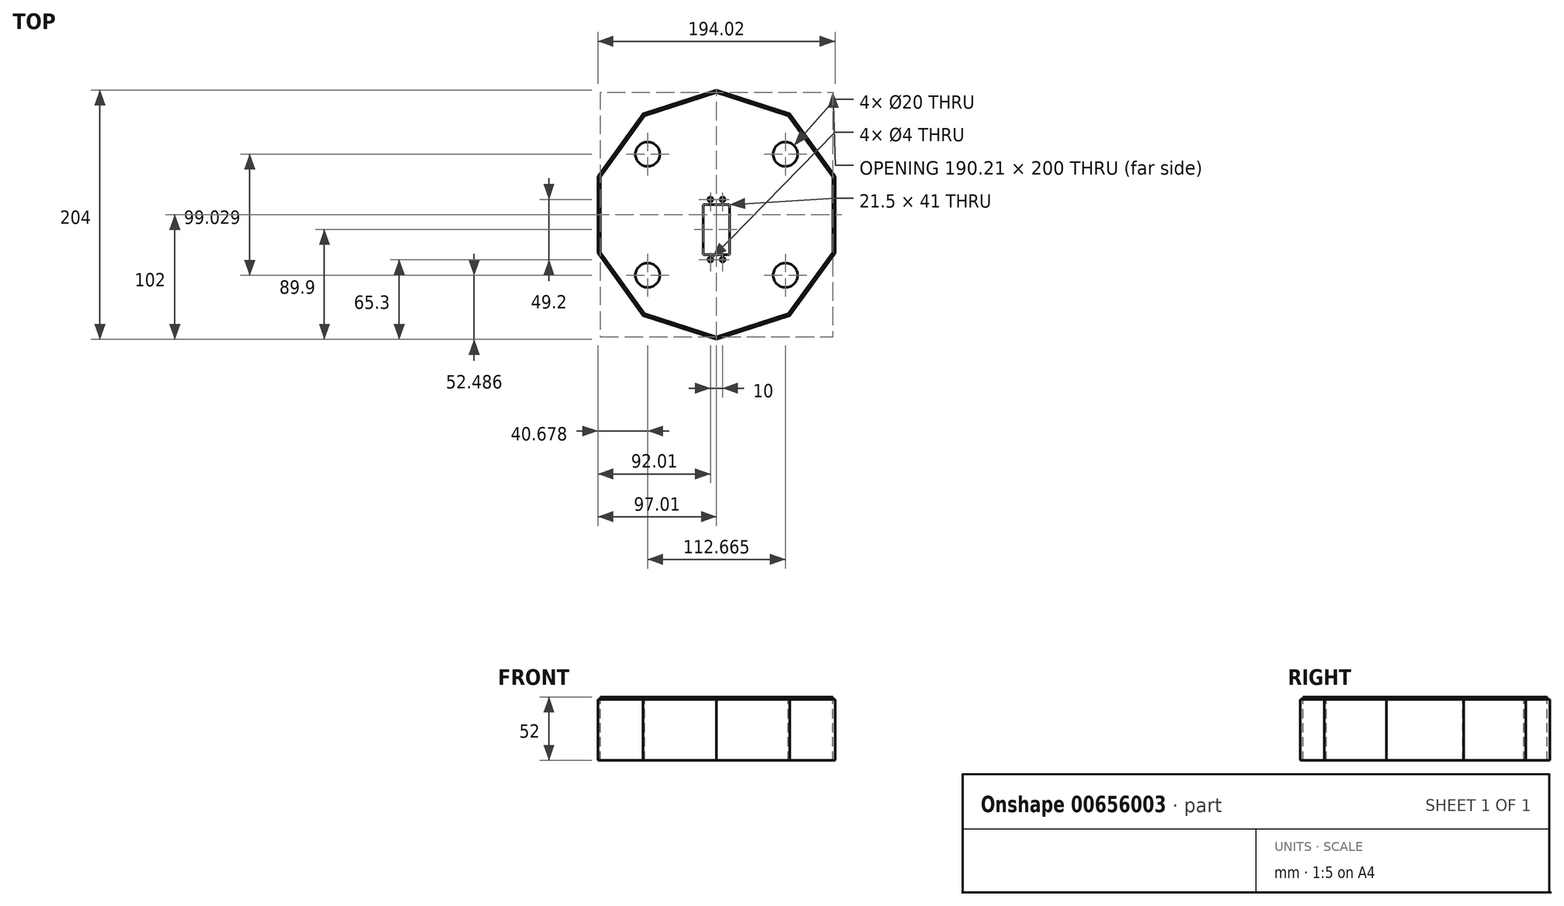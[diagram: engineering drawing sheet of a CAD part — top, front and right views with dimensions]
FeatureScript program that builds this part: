
annotation { "Feature Type Name" : "Feature", "Feature Type Description" : "" }
export const myFeature = defineFeature(function(context is Context, id is Id, definition is map)
    precondition{}
    {
        {
            var Q0;
            Q0=qCreatedBy(makeId("Top.planeOp"),FACE);
            var sketch = newSketch(context, id + "F0", { "sketchPlane" : qUnion([Q0])});
            skCircle(sketch, "E0.cCircle", {"center": v(0, 0) * mm, "radius": 100 * mm, "construction": true});
            skLineSegment(sketch, "E0.0", {"start": v(0, 100) * mm, "end": v(58.78, 80.9) * mm});
            skLineSegment(sketch, "E0.1", {"start": v(58.78, 80.9) * mm, "end": v(95.1, 30.9) * mm});
            skLineSegment(sketch, "E0.2", {"start": v(95.1, 30.9) * mm, "end": v(95.1, -30.9) * mm});
            skLineSegment(sketch, "E0.3", {"start": v(95.1, -30.9) * mm, "end": v(58.78, -80.9) * mm});
            skLineSegment(sketch, "E0.4", {"start": v(58.78, -80.9) * mm, "end": v(0, -100) * mm});
            skLineSegment(sketch, "E0.5", {"start": v(0, -100) * mm, "end": v(-58.78, -80.9) * mm});
            skLineSegment(sketch, "E0.6", {"start": v(-58.78, -80.9) * mm, "end": v(-95.1, -30.9) * mm});
            skLineSegment(sketch, "E0.7", {"start": v(-95.1, -30.9) * mm, "end": v(-95.1, 30.9) * mm});
            skLineSegment(sketch, "E0.8", {"start": v(-95.1, 30.9) * mm, "end": v(-58.78, 80.9) * mm});
            skLineSegment(sketch, "E0.9", {"start": v(-58.78, 80.9) * mm, "end": v(0, 100) * mm});
            skLineSegment(sketch, "E1.bottom", {"start": v(-10.75, 8.4) * mm, "end": v(10.75, 8.4) * mm});
            skLineSegment(sketch, "E1.top", {"start": v(-10.75, -32.6) * mm, "end": v(10.75, -32.6) * mm});
            skLineSegment(sketch, "E1.left", {"start": v(-10.75, 8.4) * mm, "end": v(-10.75, -32.6) * mm});
            skLineSegment(sketch, "E1.right", {"start": v(10.75, 8.4) * mm, "end": v(10.75, -32.6) * mm});
            skCircle(sketch, "E2", {"center": v(-5, 12.5) * mm, "radius": 2 * mm});
            skCircle(sketch, "E3", {"center": v(5, 12.5) * mm, "radius": 2 * mm});
            skCircle(sketch, "E4", {"center": v(-5, -36.7) * mm, "radius": 2 * mm});
            skCircle(sketch, "E5", {"center": v(5, -36.7) * mm, "radius": 2 * mm});
            skCircle(sketch, "E6", {"center": v(-56.33, 49.51) * mm, "radius": 10 * mm});
            skCircle(sketch, "E7", {"center": v(56.33, 49.51) * mm, "radius": 10 * mm});
            skCircle(sketch, "E8", {"center": v(-56.33, -49.51) * mm, "radius": 10 * mm});
            skCircle(sketch, "E9", {"center": v(56.33, -49.51) * mm, "radius": 10 * mm});
            skCircle(sketch, "E10.cCircle", {"center": v(0, 0) * mm, "radius": 102 * mm, "construction": true});
            skLineSegment(sketch, "E10.0", {"start": v(0, 102) * mm, "end": v(59.95, 82.52) * mm});
            skLineSegment(sketch, "E10.1", {"start": v(59.95, 82.52) * mm, "end": v(97, 31.52) * mm});
            skLineSegment(sketch, "E10.2", {"start": v(97, 31.52) * mm, "end": v(97, -31.52) * mm});
            skLineSegment(sketch, "E10.3", {"start": v(97, -31.52) * mm, "end": v(59.95, -82.52) * mm});
            skLineSegment(sketch, "E10.4", {"start": v(59.95, -82.52) * mm, "end": v(0, -102) * mm});
            skLineSegment(sketch, "E10.5", {"start": v(0, -102) * mm, "end": v(-59.95, -82.52) * mm});
            skLineSegment(sketch, "E10.6", {"start": v(-59.95, -82.52) * mm, "end": v(-97, -31.52) * mm});
            skLineSegment(sketch, "E10.7", {"start": v(-97, -31.52) * mm, "end": v(-97, 31.52) * mm});
            skLineSegment(sketch, "E10.8", {"start": v(-97, 31.52) * mm, "end": v(-59.95, 82.52) * mm});
            skLineSegment(sketch, "E10.9", {"start": v(-59.95, 82.52) * mm, "end": v(0, 102) * mm});
            skPoint(sketch, "E11", {"position": v(0, -12.1) * mm});
            skSolve(sketch);
        }
        {
            var Q0;
            Q0=makeQuery(id+"F0.imprint","IMPRINT",FACE,{"disambiguationData":[TD([[makeQuery(id+"F0.imprint","IMPRINT",EDGE,{"derivedFrom":sQuery(id+"F0.wireOp",EDGE,"E0.0")}),-1.0]])]});
            extrude(context, id + "F1", {"entities" : qUnion([Q0]), "depth" : 2 * mm, "offsetDistance" : 25 * mm});
        }
        {
            var Q0;
            Q0=qSketchRegion(id+"F0",true);
            extrude(context, id + "F2", {"entities" : qUnion([Q0]), "depth" : -50 * mm, "offsetDistance" : 25 * mm});
        }
    });
